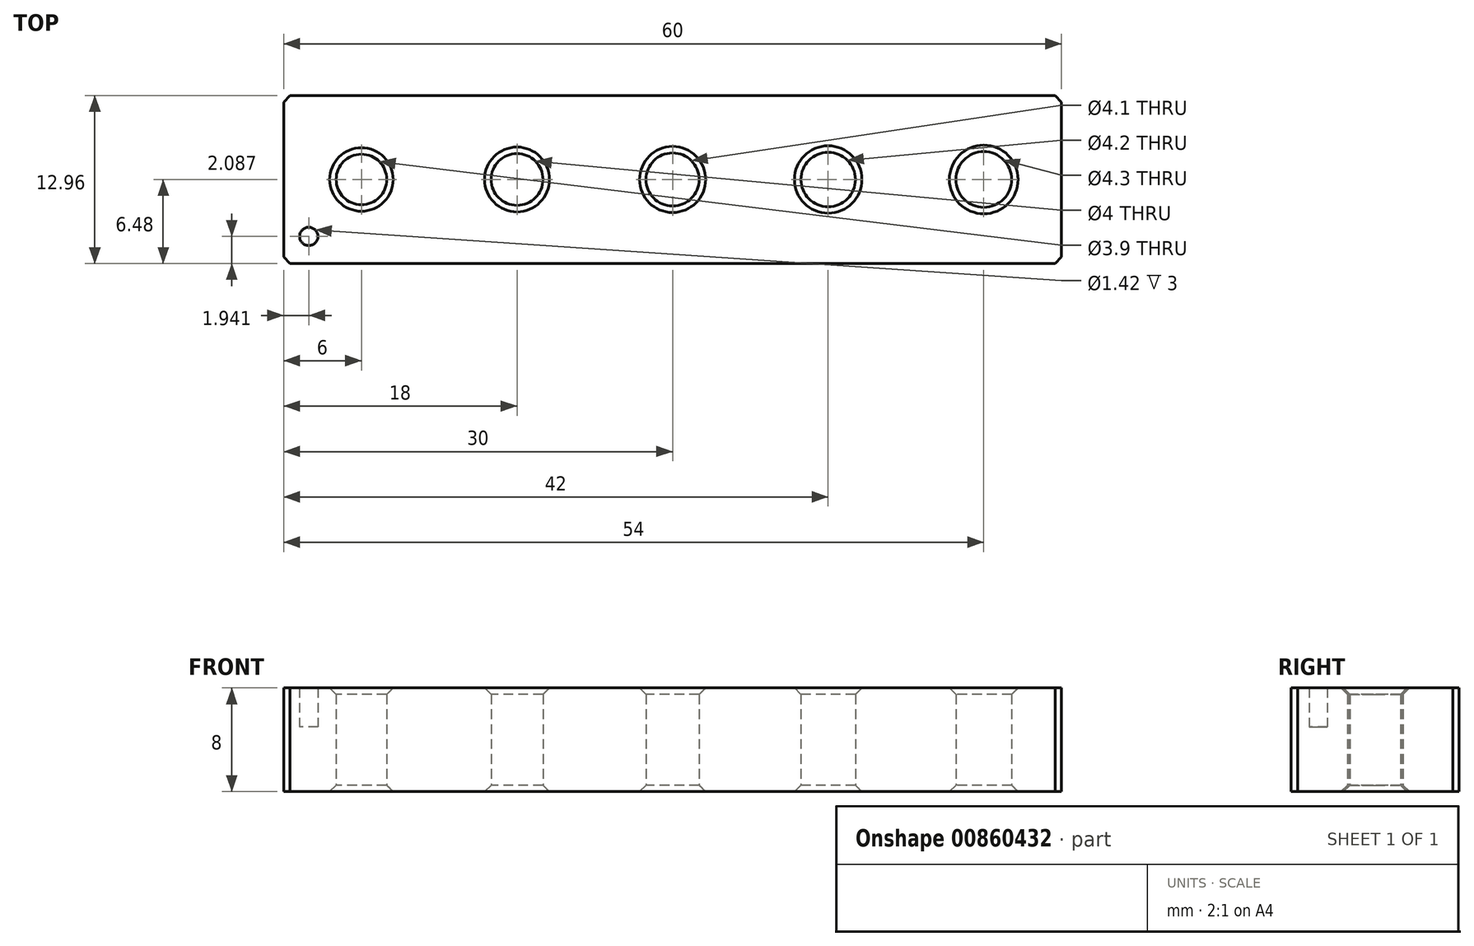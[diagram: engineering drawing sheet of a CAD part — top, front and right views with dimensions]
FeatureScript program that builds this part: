
annotation { "Feature Type Name" : "Feature", "Feature Type Description" : "" }
export const myFeature = defineFeature(function(context is Context, id is Id, definition is map)
    precondition{}
    {
        {
            var Q0;
            Q0=qCreatedBy(makeId("Top.planeOp"),FACE);
            var sketch = newSketch(context, id + "F0", { "sketchPlane" : qUnion([Q0])});
            skPoint(sketch, "E0", {"position": v(-12, 0) * mm});
            skPoint(sketch, "E1", {"position": v(-24, 0) * mm});
            skPoint(sketch, "E2", {"position": v(12, 0) * mm});
            skPoint(sketch, "E3", {"position": v(24, 0) * mm});
            skCircle(sketch, "E4", {"center": v(0, 0) * mm, "radius": 2.05 * mm});
            skCircle(sketch, "E5", {"center": v(12, 0) * mm, "radius": 2.1 * mm});
            skCircle(sketch, "E6", {"center": v(24, 0) * mm, "radius": 2.15 * mm});
            skCircle(sketch, "E7", {"center": v(-12, 0) * mm, "radius": 2 * mm});
            skCircle(sketch, "E8", {"center": v(-24, 0) * mm, "radius": 1.95 * mm});
            skLineSegment(sketch, "E9.bottom", {"start": v(30, -6.48) * mm, "end": v(-30, -6.48) * mm});
            skLineSegment(sketch, "E9.top", {"start": v(30, 6.48) * mm, "end": v(-30, 6.48) * mm});
            skLineSegment(sketch, "E9.left", {"start": v(30, -6.48) * mm, "end": v(30, 6.48) * mm});
            skLineSegment(sketch, "E9.right", {"start": v(-30, -6.48) * mm, "end": v(-30, 6.48) * mm});
            skCircle(sketch, "E10", {"center": v(-28.06, -4.4) * mm, "radius": 0.7 * mm});
            skSolve(sketch);
        }
        {
            var Q0;
            Q0=makeQuery(id+"F0.imprint","IMPRINT",FACE,{"disambiguationData":[TD([[makeQuery(id+"F0.imprint","IMPRINT",EDGE,{"derivedFrom":sQuery(id+"F0.wireOp",EDGE,"E4")}),-1.0]])]});
            extrude(context, id + "F1", {"entities" : qUnion([Q0]), "depth" : 8 * mm, "offsetDistance" : 25 * mm});
        }
        {
            var Q0;
            Q0=makeQuery(id+"F0.imprint","IMPRINT",FACE,{"disambiguationData":[TD([[makeQuery(id+"F0.imprint","IMPRINT",EDGE,{"derivedFrom":sQuery(id+"F0.wireOp",EDGE,"E10")}),1.0]])]});
            extrude(context, id + "F2", {"entities" : qUnion([Q0]), "operationType" : NewBodyOperationType.ADD, "depth" : 5 * mm, "offsetDistance" : 25 * mm});
        }
        {
            var Q0;
            Q0=makeQuery(id+"F1.opExtrude","CAP_EDGE",EDGE,{"disambiguationData":[OSD([sQuery(id+"F0.wireOp",EDGE,"E8")])],"isStart":false});
            var Q1;
            Q1=makeQuery(id+"F1.opExtrude","CAP_EDGE",EDGE,{"disambiguationData":[OSD([sQuery(id+"F0.wireOp",EDGE,"E7")])],"isStart":false});
            var Q2;
            Q2=makeQuery(id+"F1.opExtrude","CAP_EDGE",EDGE,{"disambiguationData":[OSD([sQuery(id+"F0.wireOp",EDGE,"E4")])],"isStart":false});
            var Q3;
            Q3=makeQuery(id+"F1.opExtrude","CAP_EDGE",EDGE,{"disambiguationData":[OSD([sQuery(id+"F0.wireOp",EDGE,"E5")])],"isStart":false});
            var Q4;
            Q4=makeQuery(id+"F1.opExtrude","CAP_EDGE",EDGE,{"disambiguationData":[OSD([sQuery(id+"F0.wireOp",EDGE,"E6")])],"isStart":false});
            var Q5;
            Q5=makeQuery(id+"F1.opExtrude","CAP_EDGE",EDGE,{"disambiguationData":[OSD([sQuery(id+"F0.wireOp",EDGE,"E6")])],"isStart":true});
            var Q6;
            Q6=makeQuery(id+"F1.opExtrude","CAP_EDGE",EDGE,{"disambiguationData":[OSD([sQuery(id+"F0.wireOp",EDGE,"E5")])],"isStart":true});
            var Q7;
            Q7=makeQuery(id+"F1.opExtrude","CAP_EDGE",EDGE,{"disambiguationData":[OSD([sQuery(id+"F0.wireOp",EDGE,"E4")])],"isStart":true});
            var Q8;
            Q8=makeQuery(id+"F1.opExtrude","CAP_EDGE",EDGE,{"disambiguationData":[OSD([sQuery(id+"F0.wireOp",EDGE,"E7")])],"isStart":true});
            var Q9;
            Q9=makeQuery(id+"F1.opExtrude","CAP_EDGE",EDGE,{"disambiguationData":[OSD([sQuery(id+"F0.wireOp",EDGE,"E8")])],"isStart":true});
            var Q10;
            Q10=makeQuery(id+"F1.opExtrude","SWEPT_EDGE",EDGE,{"disambiguationData":[OSD([sQuery(id+"F0.wireOp",EDGE,"E9.bottom"),sQuery(id+"F0.wireOp",EDGE,"E9.right")])]});
            var Q11;
            Q11=makeQuery(id+"F1.opExtrude","SWEPT_EDGE",EDGE,{"disambiguationData":[OSD([sQuery(id+"F0.wireOp",EDGE,"E9.top"),sQuery(id+"F0.wireOp",EDGE,"E9.right")])]});
            var Q12;
            Q12=makeQuery(id+"F1.opExtrude","SWEPT_EDGE",EDGE,{"disambiguationData":[OSD([sQuery(id+"F0.wireOp",EDGE,"E9.top"),sQuery(id+"F0.wireOp",EDGE,"E9.left")])]});
            var Q13;
            Q13=makeQuery(id+"F1.opExtrude","SWEPT_EDGE",EDGE,{"disambiguationData":[OSD([sQuery(id+"F0.wireOp",EDGE,"E9.bottom"),sQuery(id+"F0.wireOp",EDGE,"E9.left")])]});
            chamfer(context, id + "F3", {"entities" : qUnion([Q0, Q1, Q2, Q3, Q4, Q5, Q6, Q7, Q8, Q9, Q10, Q11, Q12, Q13]), "width" : 0.5 * mm, "tangentPropagation" : true});
        }
    });
